# Revit family: EKF_EE_РейкаДляКрепленияКабелейTrivia_AVERES
name_source: partatom
category: Электрооборудование
units: mm (PartAtom-declared; Revit-internal decimal feet)

## family parameters
Всегда вертикально = Нет
На основе рабочей плоскости = Да
Общий = Да
При загрузке вырезать с полостями = Нет
Размер круглого соединителя = Использовать диаметр
Тип детали = Силовой щит
Точка расчета площади = Нет

## types (4) — shared parameters
ADSK_Единица измерения = шт.
ADSK_Завод-изготовитель = EKF
ADSK_Количество = 1
ADSK_Размер_Высота = 33 мм
ADSK_Размер_Глубина = 44 мм
t1 = 1.5 мм
Высота = 33 мм
Глубина = 44 мм
Изготовитель = EKF
Серия номенклатуры = Averes
Степень защиты IP = -
ТВ = EKF_2_TRIVIA_AVERES
Тип установки = -
zero-valued in all types: ADSK_Масса, Отметка по умолчанию

## per-type parameters (varying)
| type | 300_600_800 | 400 | ADSK_Код изделия | ADSK_Марка | ADSK_Наименование | ADSK_Обозначение | ADSK_Размер_Ширина | Количество | Отступ | Отступ1 | ОтступОтв | Тип | Шаг | Ширина |
| Рейка для крепления кабелей Д800 (4шт) EKF AVERES | Да | Нет | ACR800 | Рейка для крепления кабелей Д800 (4 шт) EKF AVERES | Рейка для крепления кабелей Д800 (4 шт) EKF AVERES | Рейка для крепления кабелей Д800 (4 шт) EKF AVERES | 723 мм | 19 | 5 мм | 7.7 мм | 34.3 мм | 669 мм | 35.8 мм | 723 мм |
| Рейка для крепления кабелей Д600 (4шт) EKF AVERES | Да | Нет | ACR600 | Рейка для крепления кабелей Д600 (4 шт) EKF AVERES | Рейка для крепления кабелей Д600 (4 шт) EKF AVERES | Рейка для крепления кабелей Д600 (4 шт) EKF AVERES | 523 мм | 16 | 5 мм | 7.7 мм | 24.5 мм | 668 мм | 30.8 мм | 523 мм |
| Рейка для крепления кабелей Д400 (4шт) EKF AVERES | Нет | Да | ACR400 | Рейка для крепления кабелей Д400 (4 шт) EKF AVERES | Рейка для крепления кабелей Д400 (4 шт) EKF AVERES | Рейка для крепления кабелей Д400 (4 шт) EKF AVERES | 319 мм | 9 | 7.5 мм | 7 мм | 24 мм | 667 мм | 32 мм | 319 мм |
| Рейка для крепления кабелей Д300 (4шт) EKF AVERES | Да | Нет | ACR300 | Рейка для крепления кабелей Д300 (4 шт) EKF AVERES | Рейка для крепления кабелей Д300 (4 шт) EKF AVERES | Рейка для крепления кабелей Д300 (4 шт) EKF AVERES | 223 мм | 6 | 4.5 мм | 6.7 мм | 27 мм | 666 мм | 32 мм | 223 мм |
